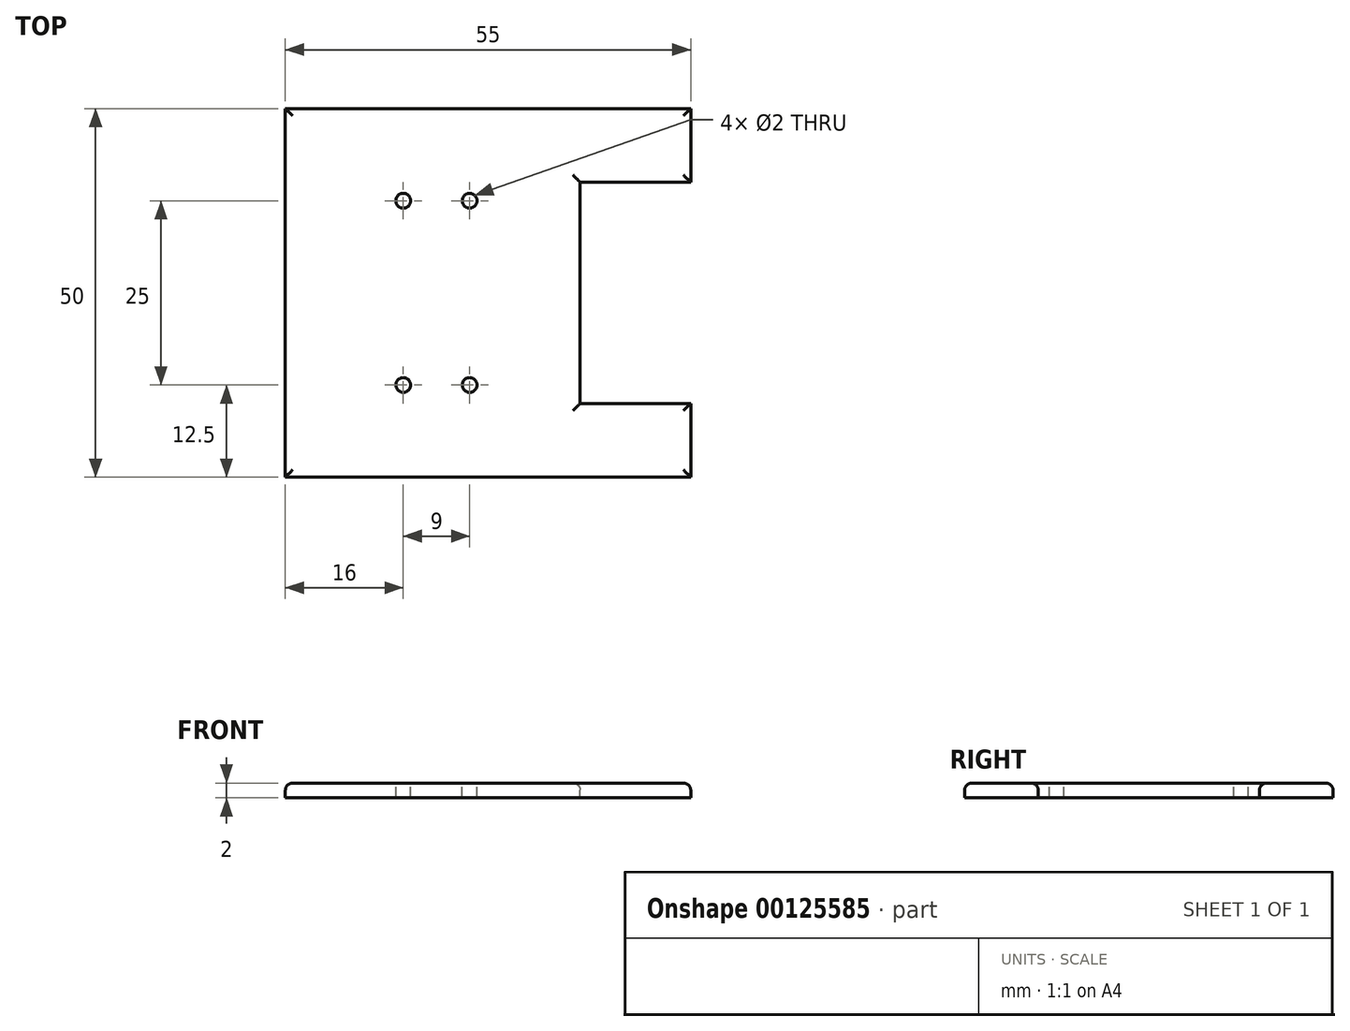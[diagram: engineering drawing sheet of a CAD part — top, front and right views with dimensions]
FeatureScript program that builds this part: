
annotation { "Feature Type Name" : "Feature", "Feature Type Description" : "" }
export const myFeature = defineFeature(function(context is Context, id is Id, definition is map)
    precondition{}
    {
        {
            var Q0;
            Q0=qCreatedBy(makeId("Top.planeOp"),FACE);
            var sketch = newSketch(context, id + "F0", { "sketchPlane" : qUnion([Q0])});
            skLineSegment(sketch, "E0.bottom", {"start": v(20, -25) * mm, "end": v(-20, -25) * mm});
            skLineSegment(sketch, "E0.top", {"start": v(20, 25) * mm, "end": v(-20, 25) * mm});
            skLineSegment(sketch, "E0.left", {"start": v(20, -25) * mm, "end": v(20, 25) * mm});
            skLineSegment(sketch, "E0.right", {"start": v(-20, -25) * mm, "end": v(-20, 25) * mm});
            skPoint(sketch, "E0.middle", {"position": v(0, 0) * mm});
            skCircle(sketch, "E1", {"center": v(-4, 12.5) * mm, "radius": 1 * mm});
            skCircle(sketch, "E2", {"center": v(5, 12.5) * mm, "radius": 1 * mm});
            skCircle(sketch, "E3", {"center": v(-4, -12.5) * mm, "radius": 1 * mm});
            skCircle(sketch, "E4", {"center": v(5, -12.5) * mm, "radius": 1 * mm});
            skLineSegment(sketch, "E5.bottom", {"start": v(20, 25) * mm, "end": v(35, 25) * mm});
            skLineSegment(sketch, "E5.top", {"start": v(20, 15) * mm, "end": v(35, 15) * mm});
            skLineSegment(sketch, "E5.left", {"start": v(20, 25) * mm, "end": v(20, 15) * mm});
            skLineSegment(sketch, "E5.right", {"start": v(35, 25) * mm, "end": v(35, 15) * mm});
            skLineSegment(sketch, "E6.bottom", {"start": v(20, -25) * mm, "end": v(35, -25) * mm});
            skLineSegment(sketch, "E6.top", {"start": v(20, -15) * mm, "end": v(35, -15) * mm});
            skLineSegment(sketch, "E6.left", {"start": v(20, -25) * mm, "end": v(20, -15) * mm});
            skLineSegment(sketch, "E6.right", {"start": v(35, -25) * mm, "end": v(35, -15) * mm});
            skSolve(sketch);
        }
        {
            var Q0;
            Q0=makeQuery(id+"F0.imprint","IMPRINT",FACE,{"disambiguationData":[TD([[makeQuery(id+"F0.imprint","IMPRINT",EDGE,{"derivedFrom":sQuery(id+"F0.wireOp",EDGE,"1teqIkxE-H5vS-1LeK-UrZz-mUXFkpOT8qA6.bottom")}),-1.0]])]});
            var Q1;
            Q1=makeQuery(id+"F0.imprint","IMPRINT",FACE,{"disambiguationData":[TD([[makeQuery(id+"F0.imprint","IMPRINT",EDGE,{"derivedFrom":sQuery(id+"F0.wireOp",EDGE,"E0.bottom")}),-1.0]])]});
            var Q2;
            Q2=makeQuery(id+"F0.imprint","IMPRINT",FACE,{"disambiguationData":[TD([[makeQuery(id+"F0.imprint","IMPRINT",EDGE,{"derivedFrom":sQuery(id+"F0.wireOp",EDGE,"E6.bottom")}),1.0]])]});
            var Q3;
            Q3=makeQuery(id+"F0.imprint","IMPRINT",FACE,{"disambiguationData":[TD([[makeQuery(id+"F0.imprint","IMPRINT",EDGE,{"derivedFrom":sQuery(id+"F0.wireOp",EDGE,"E5.bottom")}),-1.0]])]});
            extrude(context, id + "F1", {"entities" : qUnion([Q0, Q1, Q2, Q3]), "oppositeDirection" : true, "depth" : 2 * mm});
        }
        {
            var Q0;
            Q0=makeQuery(id+"F1.opExtrude","CAP_EDGE",EDGE,{"disambiguationData":[OSD([sQuery(id+"F0.wireOp",EDGE,"E0.top"),sQuery(id+"F0.wireOp",EDGE,"E5.bottom")])],"isStart":true});
            var Q1;
            Q1=makeQuery(id+"F1.opExtrude","CAP_EDGE",EDGE,{"disambiguationData":[OSD([sQuery(id+"F0.wireOp",EDGE,"E0.right")])],"isStart":true});
            var Q2;
            Q2=makeQuery(id+"F1.opExtrude","CAP_EDGE",EDGE,{"disambiguationData":[OSD([sQuery(id+"F0.wireOp",EDGE,"E5.right")])],"isStart":true});
            var Q3;
            Q3=makeQuery(id+"F1.opExtrude","CAP_EDGE",EDGE,{"disambiguationData":[OSD([sQuery(id+"F0.wireOp",EDGE,"E5.top")])],"isStart":true});
            var Q4;
            Q4=makeQuery(id+"F1.opExtrude","CAP_EDGE",EDGE,{"disambiguationData":[OSD([sQuery(id+"F0.wireOp",EDGE,"E0.left")])],"isStart":true});
            var Q5;
            Q5=makeQuery(id+"F1.opExtrude","CAP_EDGE",EDGE,{"disambiguationData":[OSD([sQuery(id+"F0.wireOp",EDGE,"E6.top")])],"isStart":true});
            var Q6;
            Q6=makeQuery(id+"F1.opExtrude","CAP_EDGE",EDGE,{"disambiguationData":[OSD([sQuery(id+"F0.wireOp",EDGE,"E6.right")])],"isStart":true});
            var Q7;
            Q7=makeQuery(id+"F1.opExtrude","CAP_EDGE",EDGE,{"disambiguationData":[OSD([sQuery(id+"F0.wireOp",EDGE,"E0.bottom"),sQuery(id+"F0.wireOp",EDGE,"E6.bottom")])],"isStart":true});
            fillet(context, id + "F2", {"entities" : qUnion([Q0, Q1, Q2, Q3, Q4, Q5, Q6, Q7]), "radius" : 1 * mm, "tangentPropagation" : true, "allowEdgeOverflow" : false});
        }
    });
